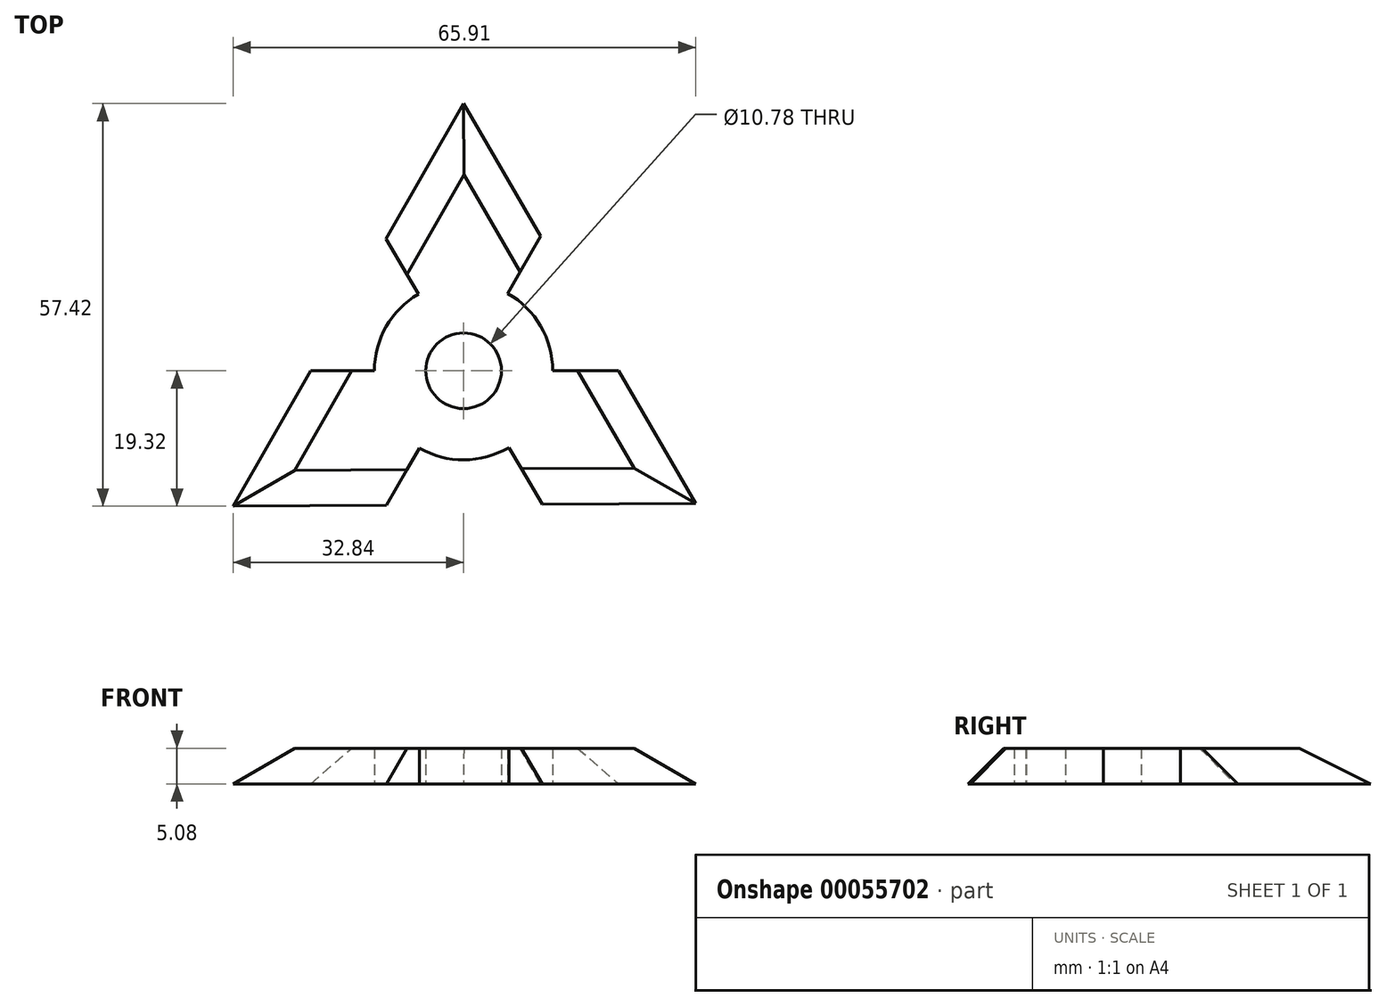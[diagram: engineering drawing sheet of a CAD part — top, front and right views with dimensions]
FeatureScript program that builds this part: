
annotation { "Feature Type Name" : "Feature", "Feature Type Description" : "" }
export const myFeature = defineFeature(function(context is Context, id is Id, definition is map)
    precondition{}
    {
        {
            var Q0;
            Q0=qCreatedBy(makeId("Top.planeOp"),FACE);
            var sketch = newSketch(context, id + "F0", { "sketchPlane" : qUnion([Q0])});
            skCircle(sketch, "E0", {"center": v(0, 0) * mm, "radius": 5.4 * mm});
            skCircle(sketch, "E1", {"center": v(0, 0) * mm, "radius": 12.7 * mm});
            skLineSegment(sketch, "E2", {"start": v(0, 0) * mm, "end": v(0, 38.1) * mm});
            skLineSegment(sketch, "E3", {"start": v(0, 0) * mm, "end": v(-32.84, -19.32) * mm});
            skLineSegment(sketch, "E4", {"start": v(0, 0) * mm, "end": v(33.07, -18.91) * mm});
            skLineSegment(sketch, "E5", {"start": v(0, 38.1) * mm, "end": v(-32.84, -19.32) * mm});
            skLineSegment(sketch, "E6", {"start": v(33.07, -18.91) * mm, "end": v(-32.84, -19.32) * mm});
            skLineSegment(sketch, "E7", {"start": v(33.07, -18.91) * mm, "end": v(0, 38.1) * mm});
            skLineSegment(sketch, "E8", {"start": v(0, 0) * mm, "end": v(-11.05, 18.78) * mm});
            skLineSegment(sketch, "E9", {"start": v(0, 0) * mm, "end": v(-21.79, 0) * mm});
            skLineSegment(sketch, "E10", {"start": v(0, 0) * mm, "end": v(10.97, 19.19) * mm});
            skLineSegment(sketch, "E11", {"start": v(0, 0) * mm, "end": v(22.1, 0) * mm});
            skLineSegment(sketch, "E12", {"start": v(0, 0) * mm, "end": v(-10.97, -19.19) * mm});
            skLineSegment(sketch, "E13", {"start": v(0, 0) * mm, "end": v(11.2, -19.05) * mm});
            skSolve(sketch);
        }
        {
            var Q0;
            {var subQ0=sQuery(id+"F0.wireOp",EDGE,"E2");var subQ1=sQuery(id+"F0.wireOp",EDGE,"E1");var subQ2=makeQuery(id+"F0.imprint","INTERSECT",VERTEX,{"derivedFrom":[subQ1,subQ0]});Q0=makeQuery(id+"F0.imprint","IMPRINT",FACE,{"disambiguationData":[TD([[makeQuery(id+"F0.imprint","IMPRINT",EDGE,{"disambiguationData":[TD([[subQ2,-1.0]])],"derivedFrom":subQ1}),-1.0]])]});}
            var Q1;
            {var subQ0=sQuery(id+"F0.wireOp",EDGE,"E10");var subQ1=sQuery(id+"F0.wireOp",EDGE,"E1");var subQ2=makeQuery(id+"F0.imprint","INTERSECT",VERTEX,{"derivedFrom":[subQ1,subQ0]});Q1=makeQuery(id+"F0.imprint","IMPRINT",FACE,{"disambiguationData":[TD([[makeQuery(id+"F0.imprint","IMPRINT",EDGE,{"disambiguationData":[TD([[subQ2,-1.0]])],"derivedFrom":subQ1}),-1.0]])]});}
            var Q2;
            {var subQ0=sQuery(id+"F0.wireOp",EDGE,"E2");var subQ1=sQuery(id+"F0.wireOp",EDGE,"E0");var subQ2=makeQuery(id+"F0.imprint","INTERSECT",VERTEX,{"derivedFrom":[subQ1,subQ0]});Q2=makeQuery(id+"F0.imprint","IMPRINT",FACE,{"disambiguationData":[TD([[makeQuery(id+"F0.imprint","IMPRINT",EDGE,{"disambiguationData":[TD([[subQ2,-1.0]])],"derivedFrom":subQ1}),-1.0]])]});}
            var Q3;
            {var subQ0=sQuery(id+"F0.wireOp",EDGE,"E10");var subQ1=sQuery(id+"F0.wireOp",EDGE,"E0");var subQ2=makeQuery(id+"F0.imprint","INTERSECT",VERTEX,{"derivedFrom":[subQ1,subQ0]});Q3=makeQuery(id+"F0.imprint","IMPRINT",FACE,{"disambiguationData":[TD([[makeQuery(id+"F0.imprint","IMPRINT",EDGE,{"disambiguationData":[TD([[subQ2,-1.0]])],"derivedFrom":subQ1}),-1.0]])]});}
            var Q4;
            {var subQ0=sQuery(id+"F0.wireOp",EDGE,"E8");var subQ1=sQuery(id+"F0.wireOp",EDGE,"E0");var subQ2=makeQuery(id+"F0.imprint","INTERSECT",VERTEX,{"derivedFrom":[subQ1,subQ0]});Q4=makeQuery(id+"F0.imprint","IMPRINT",FACE,{"disambiguationData":[TD([[makeQuery(id+"F0.imprint","IMPRINT",EDGE,{"disambiguationData":[TD([[subQ2,-1.0]])],"derivedFrom":subQ1}),-1.0]])]});}
            var Q5;
            {var subQ0=sQuery(id+"F0.wireOp",EDGE,"E10");var subQ1=sQuery(id+"F0.wireOp",EDGE,"E0");var subQ2=makeQuery(id+"F0.imprint","INTERSECT",VERTEX,{"derivedFrom":[subQ1,subQ0]});Q5=makeQuery(id+"F0.imprint","IMPRINT",FACE,{"disambiguationData":[TD([[makeQuery(id+"F0.imprint","IMPRINT",EDGE,{"disambiguationData":[TD([[subQ2,1.0]])],"derivedFrom":subQ1}),-1.0]])]});}
            var Q6;
            {var subQ0=sQuery(id+"F0.wireOp",EDGE,"E9");var subQ1=sQuery(id+"F0.wireOp",EDGE,"E0");var subQ2=makeQuery(id+"F0.imprint","INTERSECT",VERTEX,{"derivedFrom":[subQ1,subQ0]});Q6=makeQuery(id+"F0.imprint","IMPRINT",FACE,{"disambiguationData":[TD([[makeQuery(id+"F0.imprint","IMPRINT",EDGE,{"disambiguationData":[TD([[subQ2,-1.0]])],"derivedFrom":subQ1}),-1.0]])]});}
            var Q7;
            {var subQ0=sQuery(id+"F0.wireOp",EDGE,"E11");var subQ1=sQuery(id+"F0.wireOp",EDGE,"E0");var subQ2=makeQuery(id+"F0.imprint","INTERSECT",VERTEX,{"derivedFrom":[subQ1,subQ0]});Q7=makeQuery(id+"F0.imprint","IMPRINT",FACE,{"disambiguationData":[TD([[makeQuery(id+"F0.imprint","IMPRINT",EDGE,{"disambiguationData":[TD([[subQ2,1.0]])],"derivedFrom":subQ1}),-1.0]])]});}
            var Q8;
            {var subQ0=sQuery(id+"F0.wireOp",EDGE,"E13");var subQ1=sQuery(id+"F0.wireOp",EDGE,"E0");var subQ2=makeQuery(id+"F0.imprint","INTERSECT",VERTEX,{"derivedFrom":[subQ1,subQ0]});Q8=makeQuery(id+"F0.imprint","IMPRINT",FACE,{"disambiguationData":[TD([[makeQuery(id+"F0.imprint","IMPRINT",EDGE,{"disambiguationData":[TD([[subQ2,-1.0]])],"derivedFrom":subQ1}),-1.0]])]});}
            var Q9;
            {var subQ0=sQuery(id+"F0.wireOp",EDGE,"E12");var subQ1=sQuery(id+"F0.wireOp",EDGE,"E0");var subQ2=makeQuery(id+"F0.imprint","INTERSECT",VERTEX,{"derivedFrom":[subQ1,subQ0]});Q9=makeQuery(id+"F0.imprint","IMPRINT",FACE,{"disambiguationData":[TD([[makeQuery(id+"F0.imprint","IMPRINT",EDGE,{"disambiguationData":[TD([[subQ2,-1.0]])],"derivedFrom":subQ1}),-1.0]])]});}
            var Q10;
            {var subQ0=sQuery(id+"F0.wireOp",EDGE,"E3");var subQ1=sQuery(id+"F0.wireOp",EDGE,"E0");var subQ2=makeQuery(id+"F0.imprint","INTERSECT",VERTEX,{"derivedFrom":[subQ1,subQ0]});Q10=makeQuery(id+"F0.imprint","IMPRINT",FACE,{"disambiguationData":[TD([[makeQuery(id+"F0.imprint","IMPRINT",EDGE,{"disambiguationData":[TD([[subQ2,-1.0]])],"derivedFrom":subQ1}),-1.0]])]});}
            var Q11;
            {var subQ0=sQuery(id+"F0.wireOp",EDGE,"E9");var subQ1=sQuery(id+"F0.wireOp",EDGE,"E1");var subQ2=makeQuery(id+"F0.imprint","INTERSECT",VERTEX,{"derivedFrom":[subQ1,subQ0]});Q11=makeQuery(id+"F0.imprint","IMPRINT",FACE,{"disambiguationData":[TD([[makeQuery(id+"F0.imprint","IMPRINT",EDGE,{"disambiguationData":[TD([[subQ2,-1.0]])],"derivedFrom":subQ1}),-1.0]])]});}
            var Q12;
            {var subQ0=sQuery(id+"F0.wireOp",EDGE,"E3");var subQ1=sQuery(id+"F0.wireOp",EDGE,"E1");var subQ2=makeQuery(id+"F0.imprint","INTERSECT",VERTEX,{"derivedFrom":[subQ1,subQ0]});Q12=makeQuery(id+"F0.imprint","IMPRINT",FACE,{"disambiguationData":[TD([[makeQuery(id+"F0.imprint","IMPRINT",EDGE,{"disambiguationData":[TD([[subQ2,-1.0]])],"derivedFrom":subQ1}),-1.0]])]});}
            var Q13;
            {var subQ0=sQuery(id+"F0.wireOp",EDGE,"E13");var subQ1=sQuery(id+"F0.wireOp",EDGE,"E1");var subQ2=makeQuery(id+"F0.imprint","INTERSECT",VERTEX,{"derivedFrom":[subQ1,subQ0]});Q13=makeQuery(id+"F0.imprint","IMPRINT",FACE,{"disambiguationData":[TD([[makeQuery(id+"F0.imprint","IMPRINT",EDGE,{"disambiguationData":[TD([[subQ2,-1.0]])],"derivedFrom":subQ1}),-1.0]])]});}
            var Q14;
            {var subQ0=sQuery(id+"F0.wireOp",EDGE,"E11");var subQ1=sQuery(id+"F0.wireOp",EDGE,"E1");var subQ2=makeQuery(id+"F0.imprint","INTERSECT",VERTEX,{"derivedFrom":[subQ1,subQ0]});Q14=makeQuery(id+"F0.imprint","IMPRINT",FACE,{"disambiguationData":[TD([[makeQuery(id+"F0.imprint","IMPRINT",EDGE,{"disambiguationData":[TD([[subQ2,1.0]])],"derivedFrom":subQ1}),-1.0]])]});}
            extrude(context, id + "F1", {"entities" : qUnion([Q0, Q1, Q2, Q3, Q4, Q5, Q6, Q7, Q8, Q9, Q10, Q11, Q12, Q13, Q14]), "depth" : 5.08 * mm});
        }
        {
            var Q0;
            {var subQ0=sQuery(id+"F0.wireOp",EDGE,"E5");Q0=makeQuery(id+"F1.opExtrude","CAP_EDGE",EDGE,{"disambiguationData":[OSD([subQ0]),TDD([makeQuery(id+"F0.imprint","IMPRINT",EDGE,{"disambiguationData":[TD([[makeQuery(id+"F0.imprint","INTERSECT",VERTEX,{"derivedFrom":[subQ0,sQuery(id+"F0.wireOp",EDGE,"E8")]}),1.0]])],"derivedFrom":subQ0})])],"isStart":false});}
            var Q1;
            {var subQ0=sQuery(id+"F0.wireOp",EDGE,"E7");Q1=makeQuery(id+"F1.opExtrude","CAP_EDGE",EDGE,{"disambiguationData":[OSD([subQ0]),TDD([makeQuery(id+"F0.imprint","IMPRINT",EDGE,{"disambiguationData":[TD([[makeQuery(id+"F0.imprint","INTERSECT",VERTEX,{"derivedFrom":[subQ0,sQuery(id+"F0.wireOp",EDGE,"E10")]}),-1.0]])],"derivedFrom":subQ0})])],"isStart":false});}
            var Q2;
            {var subQ0=sQuery(id+"F0.wireOp",EDGE,"E5");Q2=makeQuery(id+"F1.opExtrude","CAP_EDGE",EDGE,{"disambiguationData":[OSD([subQ0]),TDD([makeQuery(id+"F0.imprint","IMPRINT",EDGE,{"disambiguationData":[TD([[makeQuery(id+"F0.imprint","INTERSECT",VERTEX,{"derivedFrom":[subQ0,sQuery(id+"F0.wireOp",EDGE,"E9")]}),-1.0]])],"derivedFrom":subQ0})])],"isStart":false});}
            var Q3;
            {var subQ0=sQuery(id+"F0.wireOp",EDGE,"E6");Q3=makeQuery(id+"F1.opExtrude","CAP_EDGE",EDGE,{"disambiguationData":[OSD([subQ0]),TDD([makeQuery(id+"F0.imprint","IMPRINT",EDGE,{"disambiguationData":[TD([[makeQuery(id+"F0.imprint","INTERSECT",VERTEX,{"derivedFrom":[subQ0,sQuery(id+"F0.wireOp",EDGE,"E12")]}),-1.0]])],"derivedFrom":subQ0})])],"isStart":false});}
            var Q4;
            {var subQ0=sQuery(id+"F0.wireOp",EDGE,"E6");Q4=makeQuery(id+"F1.opExtrude","CAP_EDGE",EDGE,{"disambiguationData":[OSD([subQ0]),TDD([makeQuery(id+"F0.imprint","IMPRINT",EDGE,{"disambiguationData":[TD([[makeQuery(id+"F0.imprint","INTERSECT",VERTEX,{"derivedFrom":[subQ0,sQuery(id+"F0.wireOp",EDGE,"E13")]}),1.0]])],"derivedFrom":subQ0})])],"isStart":false});}
            var Q5;
            {var subQ0=sQuery(id+"F0.wireOp",EDGE,"E7");Q5=makeQuery(id+"F1.opExtrude","CAP_EDGE",EDGE,{"disambiguationData":[OSD([subQ0]),TDD([makeQuery(id+"F0.imprint","IMPRINT",EDGE,{"disambiguationData":[TD([[makeQuery(id+"F0.imprint","INTERSECT",VERTEX,{"derivedFrom":[subQ0,sQuery(id+"F0.wireOp",EDGE,"E11")]}),1.0]])],"derivedFrom":subQ0})])],"isStart":false});}
            chamfer(context, id + "F2", {"entities" : qUnion([Q0, Q1, Q2, Q3, Q4, Q5]), "width" : 5.08 * mm, "tangentPropagation" : true});
        }
    });
